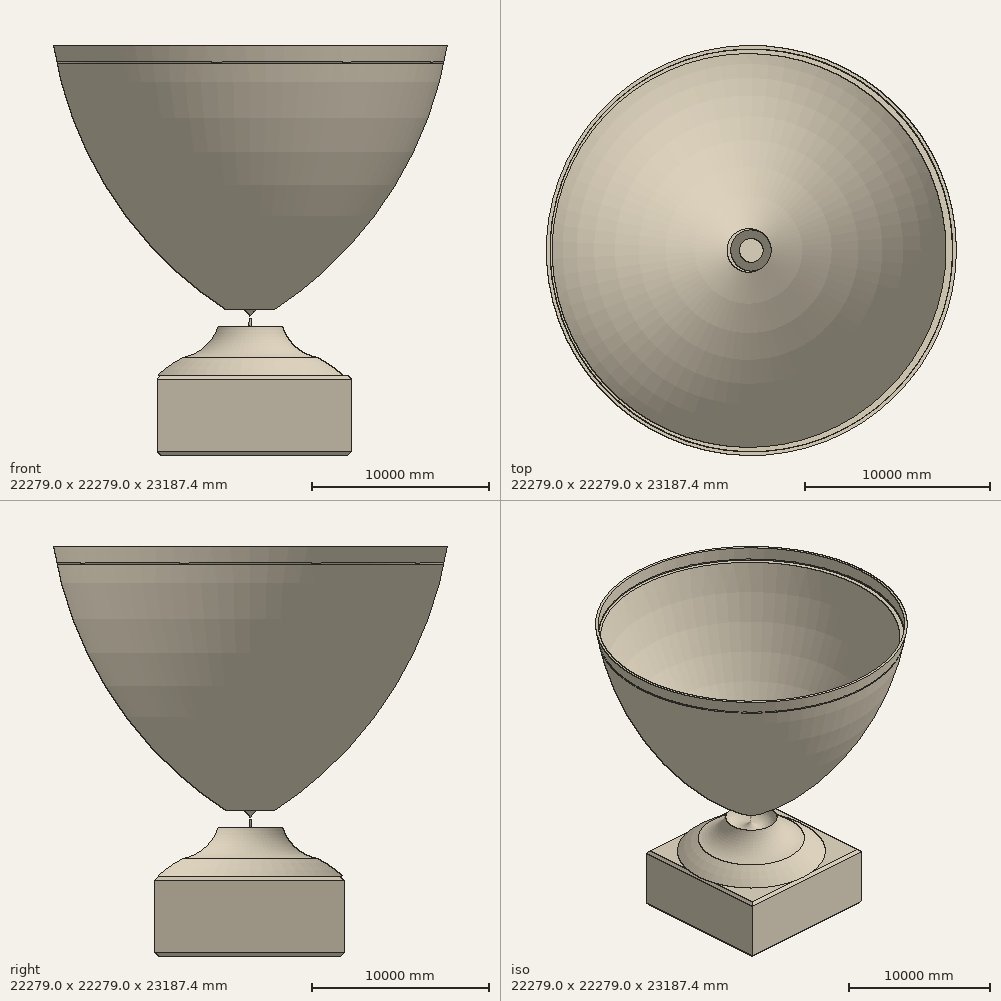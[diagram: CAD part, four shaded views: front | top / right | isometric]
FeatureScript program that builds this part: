
annotation { "Feature Type Name" : "Feature", "Feature Type Description" : "" }
export const myFeature = defineFeature(function(context is Context, id is Id, definition is map)
    precondition{}
    {
        {
            var Q0;
            Q0=qCreatedBy(makeId("Front.planeOp"),FACE);
            var sketch = newSketch(context, id + "F0", { "sketchPlane" : qUnion([Q0])});
            skLineSegment(sketch, "E0", {"start": v(-5279.6, 23.45) * mm, "end": v(5720.4, 23.45) * mm});
            skLineSegment(sketch, "E1", {"start": v(5720.4, 23.45) * mm, "end": v(5720.4, 4523.45) * mm});
            skLineSegment(sketch, "E2", {"start": v(5720.4, 4523.45) * mm, "end": v(-5279.6, 4523.45) * mm});
            skLineSegment(sketch, "E3", {"start": v(-5279.6, 4523.45) * mm, "end": v(-5279.6, 23.45) * mm});
            skSolve(sketch);
        }
        {
            var Q0;
            Q0=makeQuery(id+"F0.imprint","IMPRINT",FACE,{"disambiguationData":[TD([[makeQuery(id+"F0.imprint","IMPRINT",EDGE,{"derivedFrom":sQuery(id+"F0.wireOp",EDGE,"E0")}),1.0]])]});
            extrude(context, id + "F1", {"entities" : qUnion([Q0]), "oppositeDirection" : true, "depth" : 10700 * mm, "offsetDistance" : 25 * mm});
        }
        {
            var Q0;
            Q0=makeQuery(id+"F1.opExtrude","CAP_FACE",FACE,{"disambiguationData":[OSD([sQuery(id+"F0.wireOp",EDGE,"E0"),sQuery(id+"F0.wireOp",EDGE,"E1"),sQuery(id+"F0.wireOp",EDGE,"E2"),sQuery(id+"F0.wireOp",EDGE,"E3")])],"isStart":true});
            cPlane(context, id + "F2", {"entities" : qUnion([Q0]), "cplaneType" : CPlaneType.OFFSET, "offset" : 5400 * mm, "oppositeDirection" : true, "width" : 150 * mm, "height" : 150 * mm});
        }
        {
            var Q0;
            Q0=qCreatedBy(id+"F2.planeOp",FACE);
            var sketch = newSketch(context, id + "F3", { "sketchPlane" : qUnion([Q0])});
            skPoint(sketch, "E4.visualSharp", {"position": v(-3779.6, 4523.45) * mm});
            skLineSegment(sketch, "E4.filletArc", {"start": v(-2642.1, 4523.45) * mm, "end": v(-2642.1, 4523.45) * mm});
            skLineSegment(sketch, "E5", {"start": v(5720.4, 4523.45) * mm, "end": v(4220.4, 4523.45) * mm});
            skPoint(sketch, "E6.startSnap0", {"position": v(0, 8276.6) * mm});
            skPoint(sketch, "E7.visualSharp", {"position": v(3195.73, 23.45) * mm});
            skPoint(sketch, "E8.startSnap0", {"position": v(6951.47, 3110.84) * mm});
            skPoint(sketch, "E9.startSnap0", {"position": v(-1038.48, 7182.1) * mm});
            skLineSegment(sketch, "E10", {"start": v(-11139.51, 23210.84) * mm, "end": v(0, 23210.84) * mm});
            skLineSegment(sketch, "E11", {"start": v(0, 23210.84) * mm, "end": v(0, 6.32) * mm});
            skLineSegment(sketch, "E12", {"start": v(0, 4540.13) * mm, "end": v(-5279.6, 4523.45) * mm});
            skArc(sketch, "E13", {"start": v(-1391.82, 8276.6) * mm, "mid": v(-695.91, 8189.85) * mm, "end": v(0, 8276.6) * mm});
            skArc(sketch, "E14", {"start": v(-11139.51, 23210.84) * mm, "mid": v(-7841, 14715.5) * mm, "end": v(-1391.82, 8276.6) * mm});
            skArc(sketch, "E15", {"start": v(-1391.82, 8276.6) * mm, "mid": v(-1761.68, 7852.48) * mm, "end": v(-1831.5, 7294.09) * mm});
            skArc(sketch, "E16", {"start": v(-3792.13, 5570.6) * mm, "mid": v(-2573.64, 6161.4) * mm, "end": v(-1831.5, 7294.09) * mm});
            skArc(sketch, "E17", {"start": v(-3792.13, 5570.6) * mm, "mid": v(-4570.03, 5095.57) * mm, "end": v(-5279.6, 4523.45) * mm});
            skSolve(sketch);
        }
        {
            var Q0;
            Q0 = qSketchRegion(id + "F3", true);
            var Q1;
            Q1=sQuery(id+"F3.wireOp",EDGE,"E11");
            revolve(context, id + "F4", {"entities" : qUnion([Q0]), "axis" : qUnion([Q1]), "revolveType" : RevolveType.FULL});
        }
        {
            var Q0;
            Q0=qCreatedBy(id+"F2.planeOp",FACE);
            var sketch = newSketch(context, id + "F5", { "sketchPlane" : qUnion([Q0])});
            skLineSegment(sketch, "E18", {"start": v(0, 23365.83) * mm, "end": v(0, 8391.8) * mm});
            skLineSegment(sketch, "E19", {"start": v(-124.61, 8391.8) * mm, "end": v(-1311.53, 8391.8) * mm});
            skArc(sketch, "E20", {"start": v(-10986.8, 23040.71) * mm, "mid": v(-7653.96, 14722.37) * mm, "end": v(-1311.53, 8391.8) * mm});
            skLineSegment(sketch, "E21", {"start": v(-10986.8, 23040.71) * mm, "end": v(0, 23040.71) * mm});
            skLineSegment(sketch, "E22", {"start": v(-124.61, 23040.71) * mm, "end": v(-124.61, 8391.8) * mm});
            skPoint(sketch, "E22.endSnap0", {"position": v(-655.77, 8391.8) * mm});
            skSolve(sketch);
        }
        {
            var Q0;
            Q0 = qSketchRegion(id + "F5", true);
            var Q1;
            Q1=sQuery(id+"F5.wireOp",EDGE,"E22");
            revolve(context, id + "F6", {"operationType" : NewBodyOperationType.REMOVE, "entities" : qUnion([Q0]), "axis" : qUnion([Q1]), "revolveType" : RevolveType.FULL, "oppositeDirection" : true});
        }
        {
            var Q0;
            Q0=makeQuery(id+"F4.opRevolve","SWEPT_FACE",FACE,{"disambiguationData":[OSD([sQuery(id+"F3.wireOp",EDGE,"E10")])]});
            var sketch = newSketch(context, id + "F7", { "sketchPlane" : qUnion([Q0])});
            skCircle(sketch, "E23", {"center": v(0, 5400) * mm, "radius": 10945.78 * mm});
            skSolve(sketch);
        }
        {
            var Q0;
            Q0=makeQuery(id+"F7.imprint","IMPRINT",FACE,{"disambiguationData":[TD([[makeQuery(id+"F7.imprint","IMPRINT",EDGE,{"derivedFrom":sQuery(id+"F7.wireOp",EDGE,"E23")}),1.0]])]});
            extrude(context, id + "F8", {"entities" : qUnion([Q0]), "operationType" : NewBodyOperationType.REMOVE, "oppositeDirection" : true, "depth" : 1000 * mm, "offsetDistance" : 25 * mm});
        }
        {
            var Q0;
            Q0=makeQuery(id+"F1.opExtrude","SWEPT_EDGE",EDGE,{"disambiguationData":[OSD([sQuery(id+"F0.wireOp",EDGE,"E1"),sQuery(id+"F0.wireOp",EDGE,"E2")])]});
            var Q1;
            Q1=makeQuery(id+"F1.opExtrude","CAP_EDGE",EDGE,{"disambiguationData":[OSD([sQuery(id+"F0.wireOp",EDGE,"E2")])],"isStart":true});
            var Q2;
            Q2=makeQuery(id+"F1.opExtrude","CAP_EDGE",EDGE,{"disambiguationData":[OSD([sQuery(id+"F0.wireOp",EDGE,"E2")])],"isStart":false});
            var Q3;
            Q3=makeQuery(id+"F1.opExtrude","SWEPT_EDGE",EDGE,{"disambiguationData":[OSD([sQuery(id+"F0.wireOp",EDGE,"E2"),sQuery(id+"F0.wireOp",EDGE,"E3")])]});
            chamfer(context, id + "F9", {"entities" : qUnion([Q0, Q1, Q2, Q3]), "width" : 200 * mm, "tangentPropagation" : true});
        }
        {
            var Q0;
            Q0=makeQuery(id+"F1.opExtrude","SWEPT_EDGE",EDGE,{"disambiguationData":[OSD([sQuery(id+"F0.wireOp",EDGE,"E0"),sQuery(id+"F0.wireOp",EDGE,"E1")])]});
            var Q1;
            Q1=makeQuery(id+"F1.opExtrude","CAP_EDGE",EDGE,{"disambiguationData":[OSD([sQuery(id+"F0.wireOp",EDGE,"E0")])],"isStart":false});
            var Q2;
            Q2=makeQuery(id+"F1.opExtrude","SWEPT_EDGE",EDGE,{"disambiguationData":[OSD([sQuery(id+"F0.wireOp",EDGE,"E0"),sQuery(id+"F0.wireOp",EDGE,"E3")])]});
            var Q3;
            Q3=makeQuery(id+"F1.opExtrude","CAP_EDGE",EDGE,{"disambiguationData":[OSD([sQuery(id+"F0.wireOp",EDGE,"E0")])],"isStart":true});
            chamfer(context, id + "F10", {"entities" : qUnion([Q0, Q1, Q2, Q3]), "width" : 200 * mm, "tangentPropagation" : true});
        }
    });
